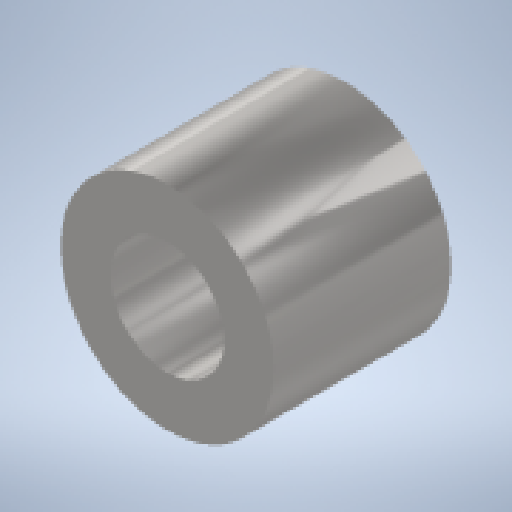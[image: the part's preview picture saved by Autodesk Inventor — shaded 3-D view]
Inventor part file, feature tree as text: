
AUTODESK INVENTOR PART (.ipt)
format: ipt  version: 2024 (Build 280153000, 153)  size: 144,384 bytes
history: native  units: mm
features: sketch x2, other x1, extrude x1, hole x1
ambient origin geometry x8: Origin, YZ Plane, XZ Plane, XY Plane, X Axis, Y Axis, Z Axis, Center Point
bodies: Body1 (feature_tree)
feature tree (5):
  other  "ソリッド1"
  extrude  "押し出し1"  Depth=6.0mm
  hole  "穴1"  [1 undecoded]
  sketch  "スケッチ1"
  sketch  "スケッチ2"
note: 1 required parameter value undecoded (feature->parameter linkage not recoverable at this tier; creation-order binding heuristic only, values carry confidence <= 0.55)
